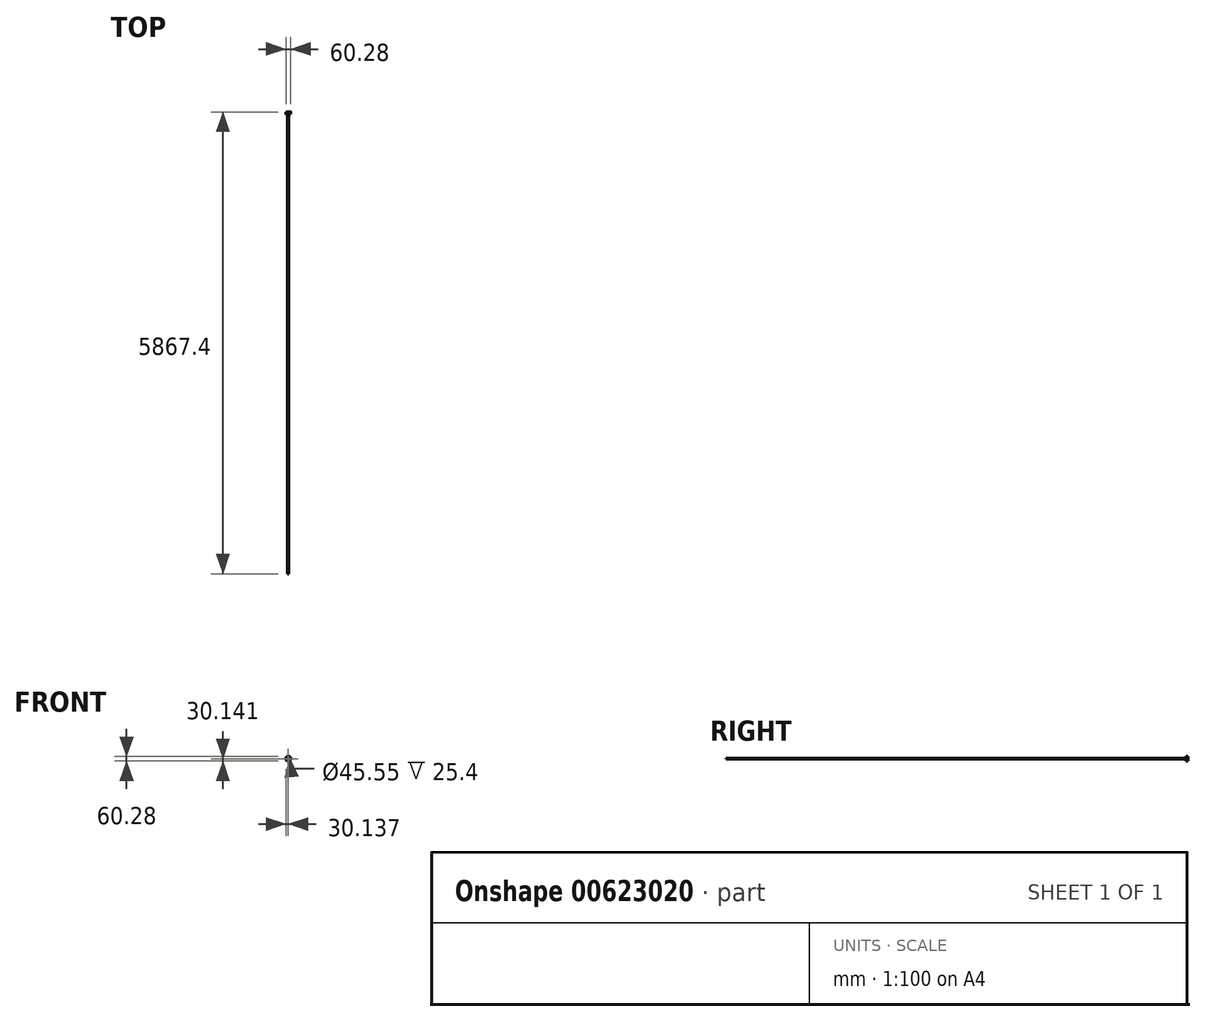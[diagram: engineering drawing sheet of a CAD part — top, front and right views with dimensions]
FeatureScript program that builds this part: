
annotation { "Feature Type Name" : "Feature", "Feature Type Description" : "" }
export const myFeature = defineFeature(function(context is Context, id is Id, definition is map)
    precondition{}
    {
        {
            var Q0;
            Q0=qCreatedBy(makeId("Front.planeOp"),FACE);
            var sketch = newSketch(context, id + "F0", { "sketchPlane" : qUnion([Q0])});
            skCircle(sketch, "E0", {"center": v(-22.7, 9.28) * mm, "radius": 30.14 * mm});
            skCircle(sketch, "E1", {"center": v(-22.7, 9.28) * mm, "radius": 22.78 * mm});
            skCircle(sketch, "E2", {"center": v(-22.7, 9.28) * mm, "radius": 11.63 * mm});
            skCircle(sketch, "E3", {"center": v(-36.41, 36.12) * mm, "radius": 2.96 * mm});
            skSolve(sketch);
        }
        {
            var Q0;
            Q0 = qSketchRegion(id + "F0", true);
            var Q1;
            Q1=makeQuery(id+"F0.imprint","IMPRINT",FACE,{"disambiguationData":[TD([[makeQuery(id+"F0.imprint","IMPRINT",EDGE,{"derivedFrom":sQuery(id+"F0.wireOp",EDGE,"E2")}),1.0]])]});
            extrude(context, id + "F1", {"entities" : qUnion([Q0, Q1]), "depth" : 25.4 * mm, "offsetDistance" : 25.4 * mm});
        }
        {
            var Q0;
            Q0=makeQuery(id+"F1.opExtrude","CAP_FACE",FACE,{"disambiguationData":[OSD([sQuery(id+"F0.wireOp",EDGE,"E2")])],"isStart":false});
            var sketch = newSketch(context, id + "F2", { "sketchPlane" : qUnion([Q0])});
            skLineSegment(sketch, "E4.bottom", {"start": v(-28.9, 14.13) * mm, "end": v(-15.94, 14.13) * mm});
            skLineSegment(sketch, "E4.top", {"start": v(-28.9, 4.05) * mm, "end": v(-15.94, 4.05) * mm});
            skLineSegment(sketch, "E4.left", {"start": v(-28.9, 14.13) * mm, "end": v(-28.9, 4.05) * mm});
            skLineSegment(sketch, "E4.right", {"start": v(-15.94, 14.13) * mm, "end": v(-15.94, 4.05) * mm});
            skSolve(sketch);
        }
        {
            var Q0;
            Q0 = qSketchRegion(id + "F2", true);
            extrude(context, id + "F3", {"entities" : qUnion([Q0]), "operationType" : NewBodyOperationType.ADD, "depth" : 5842 * mm, "offsetDistance" : 25.4 * mm});
        }
    });
